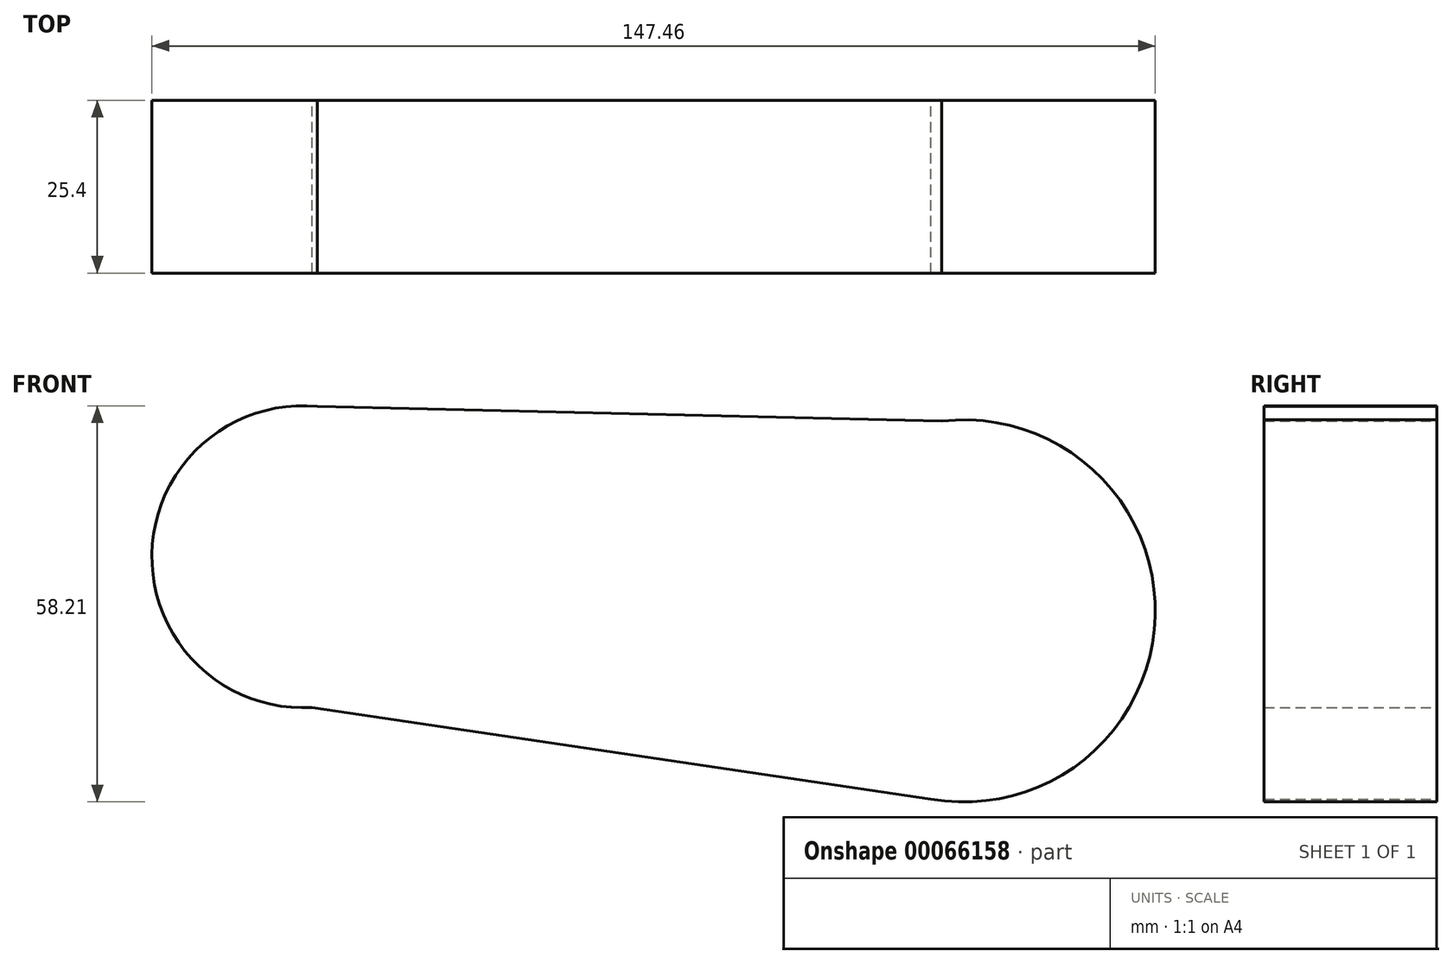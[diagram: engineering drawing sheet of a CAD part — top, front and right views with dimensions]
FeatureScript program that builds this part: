
annotation { "Feature Type Name" : "Feature", "Feature Type Description" : "" }
export const myFeature = defineFeature(function(context is Context, id is Id, definition is map)
    precondition{}
    {
        {
            var Q0;
            Q0=qCreatedBy(makeId("Front.planeOp"),FACE);
            var sketch = newSketch(context, id + "F0", { "sketchPlane" : qUnion([Q0])});
            skCircle(sketch, "E0", {"center": v(-51.59, 19.1) * mm, "radius": 22.19 * mm});
            skCircle(sketch, "E1", {"center": v(45.62, 11.15) * mm, "radius": 28.07 * mm});
            skLineSegment(sketch, "E2", {"start": v(-49.46, 41.2) * mm, "end": v(42.29, 39.03) * mm});
            skLineSegment(sketch, "E3", {"start": v(42.29, -16.72) * mm, "end": v(-50.2, -3.03) * mm});
            skLineSegment(sketch, "E4", {"start": v(9.39, -23.75) * mm, "end": v(9.39, -28.61) * mm});
            skLineSegment(sketch, "E5", {"start": v(9.39, -28.61) * mm, "end": v(14.25, -33.47) * mm});
            skLineSegment(sketch, "E6", {"start": v(14.25, -25.52) * mm, "end": v(9.39, -23.75) * mm});
            skSolve(sketch);
        }
        {
            var Q0;
            Q0 = qSketchRegion(id + "F0", true);
            extrude(context, id + "F1", {"entities" : qUnion([Q0]), "depth" : 25.4 * mm});
        }
    });
